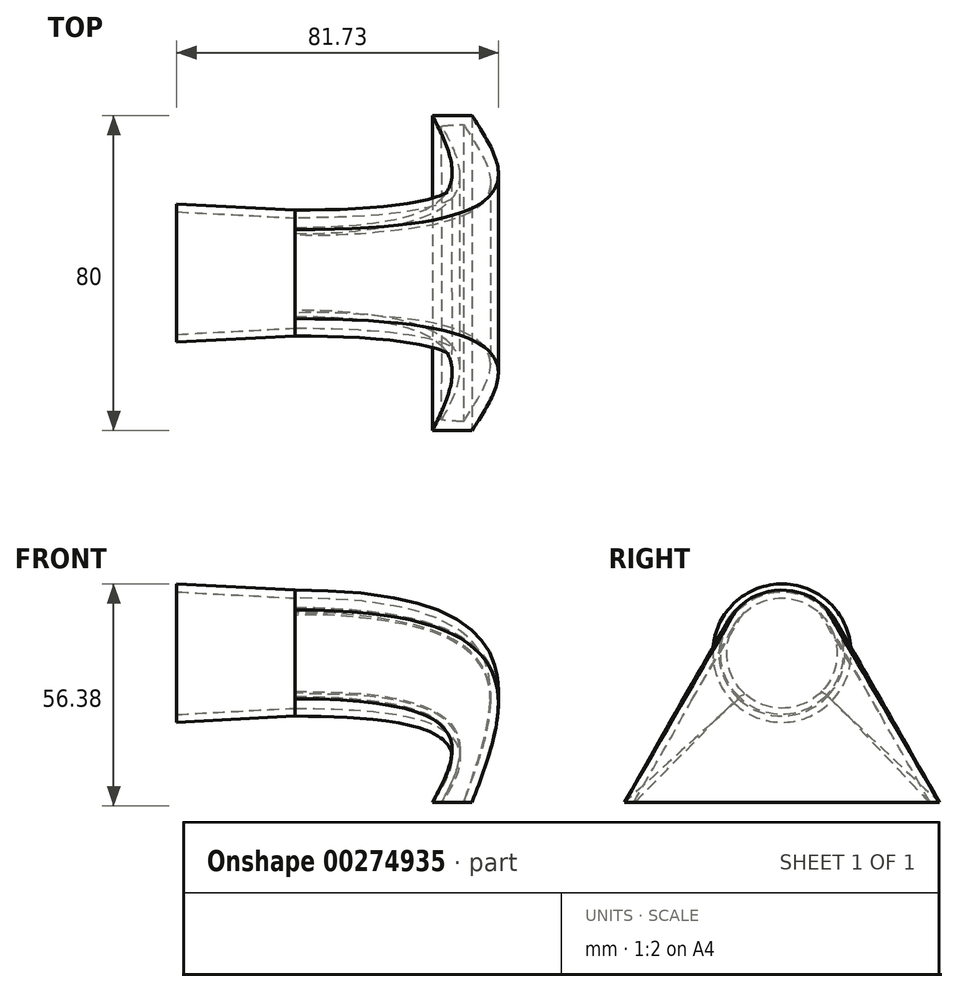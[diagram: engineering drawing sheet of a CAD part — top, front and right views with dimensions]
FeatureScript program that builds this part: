
annotation { "Feature Type Name" : "Feature", "Feature Type Description" : "" }
export const myFeature = defineFeature(function(context is Context, id is Id, definition is map)
    precondition{}
    {
        {
            var Q0;
            Q0=qCreatedBy(makeId("Right.planeOp"),FACE);
            var sketch = newSketch(context, id + "F0", { "sketchPlane" : qUnion([Q0])});
            skCircle(sketch, "E0", {"center": v(0, 37.92) * mm, "radius": 16 * mm});
            skSolve(sketch);
        }
        {
            var Q0;
            Q0=qCreatedBy(makeId("Top.planeOp"),FACE);
            var sketch = newSketch(context, id + "F1", { "sketchPlane" : qUnion([Q0])});
            skLineSegment(sketch, "E1.bottom", {"start": v(45, 40) * mm, "end": v(35, 40) * mm});
            skLineSegment(sketch, "E1.top", {"start": v(45, -40) * mm, "end": v(35, -40) * mm});
            skLineSegment(sketch, "E1.left", {"start": v(45, 40) * mm, "end": v(45, -40) * mm});
            skLineSegment(sketch, "E1.right", {"start": v(35, 40) * mm, "end": v(35, -40) * mm});
            skPoint(sketch, "E1.middle", {"position": v(40, 0) * mm});
            skSolve(sketch);
        }
        {
            var Q0;
            Q0=makeQuery(id+"F0.imprint","IMPRINT",FACE,{"disambiguationData":[TD([[makeQuery(id+"F0.imprint","IMPRINT",EDGE,{"derivedFrom":sQuery(id+"F0.wireOp",EDGE,"E0")}),1.0]])]});
            var Q1;
            Q1=makeQuery(id+"F1.imprint","IMPRINT",FACE,{"disambiguationData":[TD([[makeQuery(id+"F1.imprint","IMPRINT",EDGE,{"derivedFrom":sQuery(id+"F1.wireOp",EDGE,"E1.bottom")}),1.0]])]});
            loft(context, id + "F2", {"startCondition" : LoftEndDerivativeType.NORMAL_TO_PROFILE, "startMagnitude" : 4, "sheetProfilesArray" : [{ "sheetProfileEntities" : qUnion([Q0]) }, { "sheetProfileEntities" : qUnion([Q1]) }]});
        }
        {
            var Q0;
            Q0=makeQuery(id+"F2.opLoft","CAP_FACE",FACE,{"disambiguationData":[OSD([makeQuery(id+"F0.imprint","IMPRINT",FACE,{"disambiguationData":[TD([[makeQuery(id+"F0.imprint","IMPRINT",EDGE,{"derivedFrom":sQuery(id+"F0.wireOp",EDGE,"E0")}),1.0]])]})])],"isStart":true});
            var sketch = newSketch(context, id + "F3", { "sketchPlane" : qUnion([Q0])});
            skSolve(sketch);
        }
        {
            var Q0;
            {var subQ0=sQuery(id+"F1.wireOp",EDGE,"E1.right");var subQ1=sQuery(id+"F1.wireOp",EDGE,"E1.left");var subQ2=sQuery(id+"F1.wireOp",EDGE,"E1.bottom");var subQ3=sQuery(id+"F0.wireOp",EDGE,"E0");Q0=makeQuery(id+"F3.imprint","IMPRINT",FACE,{"disambiguationData":[TD([[makeQuery(id+"F3.imprint","IMPRINT",EDGE,{"derivedFrom":makeQuery(id+"F2.opLoft","MID_CAP_EDGE",EDGE,{"disambiguationData":[OSD([subQ3,subQ2,subQ1,subQ0]),OD(0.0)],"capPos":0.0})}),1.0]])]});}
            extrude(context, id + "F4", {"entities" : qUnion([Q0]), "operationType" : NewBodyOperationType.ADD, "depth" : 30 * mm, "hasDraft" : true, "draftAngle" : 3 * degree});
        }
        {
            var Q0;
            Q0=makeQuery(id+"F4.opExtrude","CAP_FACE",FACE,{"disambiguationData":[OSD([sQuery(id+"F0.wireOp",EDGE,"E0"),sQuery(id+"F1.wireOp",EDGE,"E1.bottom"),sQuery(id+"F1.wireOp",EDGE,"E1.top"),sQuery(id+"F1.wireOp",EDGE,"E1.left"),sQuery(id+"F1.wireOp",EDGE,"E1.right")])],"isStart":false});
            var Q1;
            Q1=makeQuery(id+"F2.opLoft","CAP_FACE",FACE,{"disambiguationData":[OSD([makeQuery(id+"F1.imprint","IMPRINT",FACE,{"disambiguationData":[TD([[makeQuery(id+"F1.imprint","IMPRINT",EDGE,{"derivedFrom":sQuery(id+"F1.wireOp",EDGE,"E1.bottom")}),1.0]])]})])],"isStart":true});
            shell(context, id + "F5", {"entities" : qUnion([Q0, Q1]), "thickness" : 2 * mm});
        }
    });
